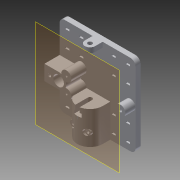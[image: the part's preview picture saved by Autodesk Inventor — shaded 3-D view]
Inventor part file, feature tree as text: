
AUTODESK INVENTOR PART (.ipt)
format: ipt  version: 2013 (Build 170138000, 138)  size: 471,552 bytes
history: native  units: in
note: dims shown in document units (in); Inventor stores cm internally (conversion verified against a paired STEP export)
features: extrude x19, sketch x19, reference x2, projected_geometry x2, plane x1, fillet x1, mirror x1
ambient origin geometry x8: Origin, YZ Plane, XZ Plane, XY Plane, X Axis, Y Axis, Z Axis, Center Point
bodies: Solid1 (feature_tree)
feature tree (45):
  extrude  "Extrusion1"  Depth=0.4921in
  extrude  "Extrusion2"  Depth=0.748in TaperAngle=0.0deg
  extrude  "Extrusion3"  Depth=1.378in TaperAngle=0.0deg
  extrude  "Extrusion4"  Depth=0.1181in
  plane  "Work Plane1"
  extrude  "Extrusion5"  Depth=1.378in TaperAngle=0.0deg
  extrude  "Extrusion6"  Depth=0.2362in
  extrude  "Extrusion7"  Depth=0.1181in TaperAngle=0.0deg
  fillet  "Fillet1"  Radius=0.0787in
  extrude  "Extrusion8"  Depth=0.0787in
  extrude  "Extrusion9"  Depth=0.1378in TaperAngle=0.0deg
  extrude  "Extrusion10"  Depth=0.1969in TaperAngle=0.0deg
  extrude  "Extrusion11"  Depth=0.1969in TaperAngle=0.0deg
  extrude  "Extrusion12"  Depth=0.5512in
  extrude  "Extrusion13"  Depth=0.5906in TaperAngle=0.0deg
  mirror  "Mirror1"
  extrude  "Extrusion14"  Depth=0.5906in TaperAngle=0.0deg
  extrude  "Extrusion15"  Depth=0.5906in TaperAngle=0.0deg
  extrude  "Extrusion16"  Depth=0.4134in TaperAngle=0.0deg
  extrude  "Extrusion17"  Depth=0.4134in TaperAngle=0.0deg
  extrude  "Extrusion18"  Depth=0.1181in
  extrude  "Extrusion19"  Depth=0.4134in TaperAngle=0.0deg
  sketch  "Sketch1"  dims[d0=0.1969in d1=0.0in d2=0.4921in]
  reference  "Reference1"
  sketch  "Sketch2"  dims[d3=0.4921in d4=0.748in d5=0.0in]
  sketch  "Sketch3"  dims[d6=0.6378in d8=1.378in d9=0.0in]
  sketch  "Sketch4"  dims[d10=0.4921in d11=0.1181in]
  sketch  "Sketch5"  dims[d12=0.5709in d13=1.378in d14=0.0in]
  projected_geometry  "Projected Loop1"
  sketch  "Sketch6"  dims[d15=0.7874in d16=0.2362in]
  projected_geometry  "Projected Loop2"
  sketch  "Sketch7"  dims[d18=1.378in d19=0.0in d20=0.1181in d21=0.0in d22=0.0787in]
  sketch  "Sketch8"  dims[d25=0.1969in d26=0.0in d27=0.0787in]
  sketch  "Sketch9"  dims[d28=0.2835in d29=0.1378in d30=0.0in]
  sketch  "Sketch10"  dims[d31=0.0827in d33=0.1969in d34=0.0in]
  sketch  "Sketch11"  dims[d35=0.1969in d38=0.1969in d39=0.0in]
  sketch  "Sketch12"  dims[d40=0.2953in d42=0.5512in]
  sketch  "Sketch13"  dims[d43=0.5906in d44=0.0in d45=0.5906in d46=0.0in]
  reference  "Reference2"
  sketch  "Sketch14"  dims[d47=0.3937in d51=0.5906in d52=0.0in]
  sketch  "Sketch15"  dims[d55=0.0787in d57=0.5906in d58=0.0in]
  sketch  "Sketch16"  dims[d59=0.4134in d61=0.4134in d62=0.0in]
  sketch  "Sketch17"  dims[d63=0.2559in d66=0.4134in d67=0.0in]
  sketch  "Sketch18"  dims[d68=0.2362in d70=0.1181in]
  sketch  "Sketch19"  dims[d71=0.1969in d72=0.4134in d73=0.0in d74=0.1181in d76=0.1969in d77=0.4134in d78=0.0in d79=0.3937in d80=0.0in]
